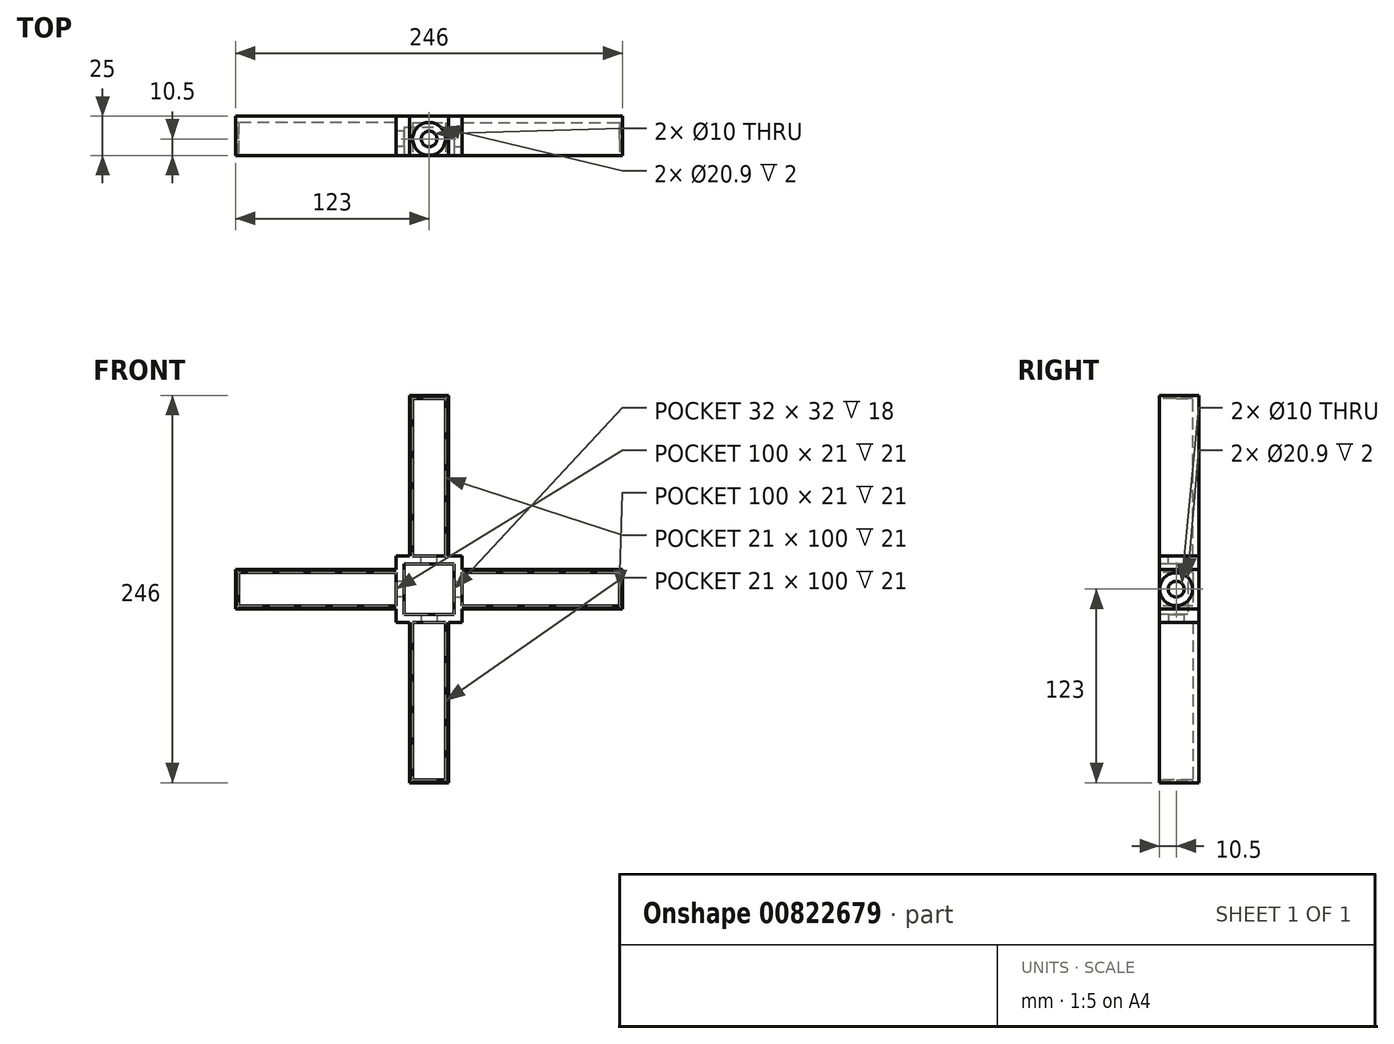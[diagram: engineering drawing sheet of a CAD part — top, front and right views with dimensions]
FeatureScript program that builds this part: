
annotation { "Feature Type Name" : "Feature", "Feature Type Description" : "" }
export const myFeature = defineFeature(function(context is Context, id is Id, definition is map)
    precondition{}
    {
        {
            var Q0;
            Q0=qCreatedBy(makeId("Front.planeOp"),FACE);
            var sketch = newSketch(context, id + "F0", { "sketchPlane" : qUnion([Q0])});
            skLineSegment(sketch, "E0.bottom", {"start": v(-21, 21) * mm, "end": v(21, 21) * mm});
            skLineSegment(sketch, "E0.top", {"start": v(-21, -21) * mm, "end": v(21, -21) * mm});
            skLineSegment(sketch, "E0.left", {"start": v(-21, 21) * mm, "end": v(-21, -21) * mm});
            skLineSegment(sketch, "E0.right", {"start": v(21, 21) * mm, "end": v(21, -21) * mm});
            skPoint(sketch, "E0.middle", {"position": v(0, 0) * mm});
            skLineSegment(sketch, "E1.bottom", {"start": v(-16, 16) * mm, "end": v(16, 16) * mm});
            skLineSegment(sketch, "E1.top", {"start": v(-16, -16) * mm, "end": v(16, -16) * mm});
            skLineSegment(sketch, "E1.left", {"start": v(-16, 16) * mm, "end": v(-16, -16) * mm});
            skLineSegment(sketch, "E1.right", {"start": v(16, 16) * mm, "end": v(16, -16) * mm});
            skSolve(sketch);
        }
        {
            var Q0;
            Q0=qCreatedBy(makeId("Front.planeOp"),FACE);
            var sketch = newSketch(context, id + "F1", { "sketchPlane" : qUnion([Q0])});
            skLineSegment(sketch, "E2.bottom", {"start": v(-12.5, -21) * mm, "end": v(12.5, -21) * mm});
            skLineSegment(sketch, "E2.top", {"start": v(-12.5, -123) * mm, "end": v(12.5, -123) * mm});
            skLineSegment(sketch, "E2.left", {"start": v(-12.5, -21) * mm, "end": v(-12.5, -123) * mm});
            skLineSegment(sketch, "E2.right", {"start": v(12.5, -21) * mm, "end": v(12.5, -123) * mm});
            skSolve(sketch);
        }
        {
            var Q0;
            Q0=qCreatedBy(makeId("Front.planeOp"),FACE);
            var sketch = newSketch(context, id + "F2", { "sketchPlane" : qUnion([Q0])});
            skLineSegment(sketch, "E3.bottom", {"start": v(-21, 12.5) * mm, "end": v(-123, 12.5) * mm});
            skLineSegment(sketch, "E3.top", {"start": v(-21, -12.5) * mm, "end": v(-123, -12.5) * mm});
            skLineSegment(sketch, "E3.left", {"start": v(-21, 12.5) * mm, "end": v(-21, -12.5) * mm});
            skLineSegment(sketch, "E3.right", {"start": v(-123, 12.5) * mm, "end": v(-123, -12.5) * mm});
            skSolve(sketch);
        }
        {
            var Q0;
            Q0=qCreatedBy(makeId("Front.planeOp"),FACE);
            var sketch = newSketch(context, id + "F3", { "sketchPlane" : qUnion([Q0])});
            skLineSegment(sketch, "E4.bottom", {"start": v(21, 12.5) * mm, "end": v(123, 12.5) * mm});
            skLineSegment(sketch, "E4.top", {"start": v(21, -12.5) * mm, "end": v(123, -12.5) * mm});
            skLineSegment(sketch, "E4.left", {"start": v(21, 12.5) * mm, "end": v(21, -12.5) * mm});
            skLineSegment(sketch, "E4.right", {"start": v(123, 12.5) * mm, "end": v(123, -12.5) * mm});
            skSolve(sketch);
        }
        {
            var Q0;
            Q0=qCreatedBy(makeId("Front.planeOp"),FACE);
            var sketch = newSketch(context, id + "F4", { "sketchPlane" : qUnion([Q0])});
            skLineSegment(sketch, "E5.bottom", {"start": v(-12.5, 21) * mm, "end": v(12.5, 21) * mm});
            skLineSegment(sketch, "E5.top", {"start": v(-12.5, 123) * mm, "end": v(12.5, 123) * mm});
            skLineSegment(sketch, "E5.left", {"start": v(-12.5, 21) * mm, "end": v(-12.5, 123) * mm});
            skLineSegment(sketch, "E5.right", {"start": v(12.5, 21) * mm, "end": v(12.5, 123) * mm});
            skSolve(sketch);
        }
        {
            var Q0;
            Q0 = qSketchRegion(id + "F0", true);
            var Q1;
            Q1=makeQuery(id+"F0.imprint","IMPRINT",FACE,{"disambiguationData":[TD([[makeQuery(id+"F0.imprint","IMPRINT",EDGE,{"derivedFrom":sQuery(id+"F0.wireOp",EDGE,"E1.bottom")}),-1.0]])]});
            extrude(context, id + "F5", {"entities" : qUnion([Q0, Q1]), "depth" : 25 * mm, "offsetDistance" : 25 * mm});
        }
        {
            var Q0;
            Q0 = qSketchRegion(id + "F1", true);
            var Q1;
            Q1 = qSketchRegion(id + "F2", true);
            var Q2;
            Q2 = qSketchRegion(id + "F3", true);
            var Q3;
            Q3 = qSketchRegion(id + "F4", true);
            extrude(context, id + "F6", {"entities" : qUnion([Q0, Q1, Q2, Q3]), "operationType" : NewBodyOperationType.ADD, "depth" : 25 * mm, "offsetDistance" : 25 * mm});
        }
        {
            var Q0;
            Q0=makeQuery(id+"F6.boolean.opBoolean","MERGE",FACE,{"derivedFrom":[makeQuery(id+"F5.opExtrude","CAP_FACE",FACE,{"disambiguationData":[OSD([sQuery(id+"F0.wireOp",EDGE,"E0.bottom"),sQuery(id+"F0.wireOp",EDGE,"E0.top"),sQuery(id+"F0.wireOp",EDGE,"E0.left"),sQuery(id+"F0.wireOp",EDGE,"E0.right")])],"isStart":false}),makeQuery(id+"F6.opExtrude","CAP_FACE",FACE,{"disambiguationData":[OSD([sQuery(id+"F1.wireOp",EDGE,"E2.bottom"),sQuery(id+"F1.wireOp",EDGE,"E2.top"),sQuery(id+"F1.wireOp",EDGE,"E2.left"),sQuery(id+"F1.wireOp",EDGE,"E2.right")])],"isStart":false}),makeQuery(id+"F6.opExtrude","CAP_FACE",FACE,{"disambiguationData":[OSD([sQuery(id+"F2.wireOp",EDGE,"E3.bottom"),sQuery(id+"F2.wireOp",EDGE,"E3.top"),sQuery(id+"F2.wireOp",EDGE,"E3.left"),sQuery(id+"F2.wireOp",EDGE,"E3.right")])],"isStart":false}),makeQuery(id+"F6.opExtrude","CAP_FACE",FACE,{"disambiguationData":[OSD([sQuery(id+"F3.wireOp",EDGE,"E4.bottom"),sQuery(id+"F3.wireOp",EDGE,"E4.top"),sQuery(id+"F3.wireOp",EDGE,"E4.left"),sQuery(id+"F3.wireOp",EDGE,"E4.right")])],"isStart":false}),makeQuery(id+"F6.opExtrude","CAP_FACE",FACE,{"disambiguationData":[OSD([sQuery(id+"F4.wireOp",EDGE,"E5.bottom"),sQuery(id+"F4.wireOp",EDGE,"E5.top"),sQuery(id+"F4.wireOp",EDGE,"E5.left"),sQuery(id+"F4.wireOp",EDGE,"E5.right")])],"isStart":false})]});
            var sketch = newSketch(context, id + "F7", { "sketchPlane" : qUnion([Q0])});
            skLineSegment(sketch, "E6.bottom", {"start": v(-16, 16) * mm, "end": v(16, 16) * mm});
            skLineSegment(sketch, "E6.top", {"start": v(-16, -16) * mm, "end": v(16, -16) * mm});
            skLineSegment(sketch, "E6.left", {"start": v(-16, 16) * mm, "end": v(-16, -16) * mm});
            skLineSegment(sketch, "E6.right", {"start": v(16, 16) * mm, "end": v(16, -16) * mm});
            skPoint(sketch, "E6.middle", {"position": v(0, 0) * mm});
            skSolve(sketch);
        }
        {
            var Q0;
            Q0=makeQuery(id+"F7.imprint","IMPRINT",FACE,{"disambiguationData":[TD([[makeQuery(id+"F7.imprint","IMPRINT",EDGE,{"derivedFrom":sQuery(id+"F7.wireOp",EDGE,"E6.bottom")}),-1.0]])]});
            extrude(context, id + "F8", {"entities" : qUnion([Q0]), "operationType" : NewBodyOperationType.REMOVE, "oppositeDirection" : true, "depth" : 18 * mm, "offsetDistance" : 25 * mm});
        }
        {
            var Q0;
            Q0=makeQuery(id+"F6.boolean.opBoolean","MERGE",FACE,{"derivedFrom":[makeQuery(id+"F5.opExtrude","CAP_FACE",FACE,{"disambiguationData":[OSD([sQuery(id+"F0.wireOp",EDGE,"E0.bottom"),sQuery(id+"F0.wireOp",EDGE,"E0.top"),sQuery(id+"F0.wireOp",EDGE,"E0.left"),sQuery(id+"F0.wireOp",EDGE,"E0.right")])],"isStart":false}),makeQuery(id+"F6.opExtrude","CAP_FACE",FACE,{"disambiguationData":[OSD([sQuery(id+"F1.wireOp",EDGE,"E2.bottom"),sQuery(id+"F1.wireOp",EDGE,"E2.top"),sQuery(id+"F1.wireOp",EDGE,"E2.left"),sQuery(id+"F1.wireOp",EDGE,"E2.right")])],"isStart":false}),makeQuery(id+"F6.opExtrude","CAP_FACE",FACE,{"disambiguationData":[OSD([sQuery(id+"F2.wireOp",EDGE,"E3.bottom"),sQuery(id+"F2.wireOp",EDGE,"E3.top"),sQuery(id+"F2.wireOp",EDGE,"E3.left"),sQuery(id+"F2.wireOp",EDGE,"E3.right")])],"isStart":false}),makeQuery(id+"F6.opExtrude","CAP_FACE",FACE,{"disambiguationData":[OSD([sQuery(id+"F3.wireOp",EDGE,"E4.bottom"),sQuery(id+"F3.wireOp",EDGE,"E4.top"),sQuery(id+"F3.wireOp",EDGE,"E4.left"),sQuery(id+"F3.wireOp",EDGE,"E4.right")])],"isStart":false}),makeQuery(id+"F6.opExtrude","CAP_FACE",FACE,{"disambiguationData":[OSD([sQuery(id+"F4.wireOp",EDGE,"E5.bottom"),sQuery(id+"F4.wireOp",EDGE,"E5.top"),sQuery(id+"F4.wireOp",EDGE,"E5.left"),sQuery(id+"F4.wireOp",EDGE,"E5.right")])],"isStart":false})]});
            var sketch = newSketch(context, id + "F9", { "sketchPlane" : qUnion([Q0])});
            skLineSegment(sketch, "E7.bottom", {"start": v(-21, 10.5) * mm, "end": v(-121, 10.5) * mm});
            skLineSegment(sketch, "E7.top", {"start": v(-21, -10.5) * mm, "end": v(-121, -10.5) * mm});
            skLineSegment(sketch, "E7.left", {"start": v(-21, 10.5) * mm, "end": v(-21, -10.5) * mm});
            skLineSegment(sketch, "E7.right", {"start": v(-121, 10.5) * mm, "end": v(-121, -10.5) * mm});
            skSolve(sketch);
        }
        {
            var Q0;
            Q0=makeQuery(id+"F9.imprint","IMPRINT",FACE,{"disambiguationData":[TD([[makeQuery(id+"F9.imprint","IMPRINT",EDGE,{"derivedFrom":sQuery(id+"F9.wireOp",EDGE,"E7.bottom")}),1.0]])]});
            extrude(context, id + "F10", {"entities" : qUnion([Q0]), "operationType" : NewBodyOperationType.REMOVE, "oppositeDirection" : true, "depth" : 21 * mm, "offsetDistance" : 25 * mm});
        }
        {
            var Q0;
            Q0=makeQuery(id+"F6.boolean.opBoolean","MERGE",FACE,{"derivedFrom":[makeQuery(id+"F5.opExtrude","CAP_FACE",FACE,{"disambiguationData":[OSD([sQuery(id+"F0.wireOp",EDGE,"E0.bottom"),sQuery(id+"F0.wireOp",EDGE,"E0.top"),sQuery(id+"F0.wireOp",EDGE,"E0.left"),sQuery(id+"F0.wireOp",EDGE,"E0.right")])],"isStart":false}),makeQuery(id+"F6.opExtrude","CAP_FACE",FACE,{"disambiguationData":[OSD([sQuery(id+"F1.wireOp",EDGE,"E2.bottom"),sQuery(id+"F1.wireOp",EDGE,"E2.top"),sQuery(id+"F1.wireOp",EDGE,"E2.left"),sQuery(id+"F1.wireOp",EDGE,"E2.right")])],"isStart":false}),makeQuery(id+"F6.opExtrude","CAP_FACE",FACE,{"disambiguationData":[OSD([sQuery(id+"F2.wireOp",EDGE,"E3.bottom"),sQuery(id+"F2.wireOp",EDGE,"E3.top"),sQuery(id+"F2.wireOp",EDGE,"E3.left"),sQuery(id+"F2.wireOp",EDGE,"E3.right")])],"isStart":false}),makeQuery(id+"F6.opExtrude","CAP_FACE",FACE,{"disambiguationData":[OSD([sQuery(id+"F3.wireOp",EDGE,"E4.bottom"),sQuery(id+"F3.wireOp",EDGE,"E4.top"),sQuery(id+"F3.wireOp",EDGE,"E4.left"),sQuery(id+"F3.wireOp",EDGE,"E4.right")])],"isStart":false}),makeQuery(id+"F6.opExtrude","CAP_FACE",FACE,{"disambiguationData":[OSD([sQuery(id+"F4.wireOp",EDGE,"E5.bottom"),sQuery(id+"F4.wireOp",EDGE,"E5.top"),sQuery(id+"F4.wireOp",EDGE,"E5.left"),sQuery(id+"F4.wireOp",EDGE,"E5.right")])],"isStart":false})]});
            var sketch = newSketch(context, id + "F11", { "sketchPlane" : qUnion([Q0])});
            skLineSegment(sketch, "E8.bottom", {"start": v(21, 10.5) * mm, "end": v(121, 10.5) * mm});
            skLineSegment(sketch, "E8.top", {"start": v(21, -10.5) * mm, "end": v(121, -10.5) * mm});
            skLineSegment(sketch, "E8.left", {"start": v(21, 10.5) * mm, "end": v(21, -10.5) * mm});
            skLineSegment(sketch, "E8.right", {"start": v(121, 10.5) * mm, "end": v(121, -10.5) * mm});
            skSolve(sketch);
        }
        {
            var Q0;
            Q0=makeQuery(id+"F11.imprint","IMPRINT",FACE,{"disambiguationData":[TD([[makeQuery(id+"F11.imprint","IMPRINT",EDGE,{"derivedFrom":sQuery(id+"F11.wireOp",EDGE,"E8.bottom")}),-1.0]])]});
            extrude(context, id + "F12", {"entities" : qUnion([Q0]), "operationType" : NewBodyOperationType.REMOVE, "oppositeDirection" : true, "depth" : 21 * mm, "offsetDistance" : 25 * mm});
        }
        {
            var Q0;
            Q0=makeQuery(id+"F6.boolean.opBoolean","MERGE",FACE,{"derivedFrom":[makeQuery(id+"F5.opExtrude","CAP_FACE",FACE,{"disambiguationData":[OSD([sQuery(id+"F0.wireOp",EDGE,"E0.bottom"),sQuery(id+"F0.wireOp",EDGE,"E0.top"),sQuery(id+"F0.wireOp",EDGE,"E0.left"),sQuery(id+"F0.wireOp",EDGE,"E0.right")])],"isStart":false}),makeQuery(id+"F6.opExtrude","CAP_FACE",FACE,{"disambiguationData":[OSD([sQuery(id+"F1.wireOp",EDGE,"E2.bottom"),sQuery(id+"F1.wireOp",EDGE,"E2.top"),sQuery(id+"F1.wireOp",EDGE,"E2.left"),sQuery(id+"F1.wireOp",EDGE,"E2.right")])],"isStart":false}),makeQuery(id+"F6.opExtrude","CAP_FACE",FACE,{"disambiguationData":[OSD([sQuery(id+"F2.wireOp",EDGE,"E3.bottom"),sQuery(id+"F2.wireOp",EDGE,"E3.top"),sQuery(id+"F2.wireOp",EDGE,"E3.left"),sQuery(id+"F2.wireOp",EDGE,"E3.right")])],"isStart":false}),makeQuery(id+"F6.opExtrude","CAP_FACE",FACE,{"disambiguationData":[OSD([sQuery(id+"F3.wireOp",EDGE,"E4.bottom"),sQuery(id+"F3.wireOp",EDGE,"E4.top"),sQuery(id+"F3.wireOp",EDGE,"E4.left"),sQuery(id+"F3.wireOp",EDGE,"E4.right")])],"isStart":false}),makeQuery(id+"F6.opExtrude","CAP_FACE",FACE,{"disambiguationData":[OSD([sQuery(id+"F4.wireOp",EDGE,"E5.bottom"),sQuery(id+"F4.wireOp",EDGE,"E5.top"),sQuery(id+"F4.wireOp",EDGE,"E5.left"),sQuery(id+"F4.wireOp",EDGE,"E5.right")])],"isStart":false})]});
            var sketch = newSketch(context, id + "F13", { "sketchPlane" : qUnion([Q0])});
            skLineSegment(sketch, "E9.bottom", {"start": v(-10.5, 21) * mm, "end": v(10.5, 21) * mm});
            skLineSegment(sketch, "E9.top", {"start": v(-10.5, 121) * mm, "end": v(10.5, 121) * mm});
            skLineSegment(sketch, "E9.left", {"start": v(-10.5, 21) * mm, "end": v(-10.5, 121) * mm});
            skLineSegment(sketch, "E9.right", {"start": v(10.5, 21) * mm, "end": v(10.5, 121) * mm});
            skSolve(sketch);
        }
        {
            var Q0;
            Q0=makeQuery(id+"F13.imprint","IMPRINT",FACE,{"disambiguationData":[TD([[makeQuery(id+"F13.imprint","IMPRINT",EDGE,{"derivedFrom":sQuery(id+"F13.wireOp",EDGE,"E9.bottom")}),1.0]])]});
            extrude(context, id + "F14", {"entities" : qUnion([Q0]), "operationType" : NewBodyOperationType.REMOVE, "oppositeDirection" : true, "depth" : 21 * mm, "offsetDistance" : 25 * mm});
        }
        {
            var Q0;
            Q0=makeQuery(id+"F6.boolean.opBoolean","MERGE",FACE,{"derivedFrom":[makeQuery(id+"F5.opExtrude","CAP_FACE",FACE,{"disambiguationData":[OSD([sQuery(id+"F0.wireOp",EDGE,"E0.bottom"),sQuery(id+"F0.wireOp",EDGE,"E0.top"),sQuery(id+"F0.wireOp",EDGE,"E0.left"),sQuery(id+"F0.wireOp",EDGE,"E0.right")])],"isStart":false}),makeQuery(id+"F6.opExtrude","CAP_FACE",FACE,{"disambiguationData":[OSD([sQuery(id+"F1.wireOp",EDGE,"E2.bottom"),sQuery(id+"F1.wireOp",EDGE,"E2.top"),sQuery(id+"F1.wireOp",EDGE,"E2.left"),sQuery(id+"F1.wireOp",EDGE,"E2.right")])],"isStart":false}),makeQuery(id+"F6.opExtrude","CAP_FACE",FACE,{"disambiguationData":[OSD([sQuery(id+"F2.wireOp",EDGE,"E3.bottom"),sQuery(id+"F2.wireOp",EDGE,"E3.top"),sQuery(id+"F2.wireOp",EDGE,"E3.left"),sQuery(id+"F2.wireOp",EDGE,"E3.right")])],"isStart":false}),makeQuery(id+"F6.opExtrude","CAP_FACE",FACE,{"disambiguationData":[OSD([sQuery(id+"F3.wireOp",EDGE,"E4.bottom"),sQuery(id+"F3.wireOp",EDGE,"E4.top"),sQuery(id+"F3.wireOp",EDGE,"E4.left"),sQuery(id+"F3.wireOp",EDGE,"E4.right")])],"isStart":false}),makeQuery(id+"F6.opExtrude","CAP_FACE",FACE,{"disambiguationData":[OSD([sQuery(id+"F4.wireOp",EDGE,"E5.bottom"),sQuery(id+"F4.wireOp",EDGE,"E5.top"),sQuery(id+"F4.wireOp",EDGE,"E5.left"),sQuery(id+"F4.wireOp",EDGE,"E5.right")])],"isStart":false})]});
            var sketch = newSketch(context, id + "F15", { "sketchPlane" : qUnion([Q0])});
            skLineSegment(sketch, "E10.bottom", {"start": v(-10.5, -21) * mm, "end": v(10.5, -21) * mm});
            skLineSegment(sketch, "E10.top", {"start": v(-10.5, -121) * mm, "end": v(10.5, -121) * mm});
            skLineSegment(sketch, "E10.left", {"start": v(-10.5, -21) * mm, "end": v(-10.5, -121) * mm});
            skLineSegment(sketch, "E10.right", {"start": v(10.5, -21) * mm, "end": v(10.5, -121) * mm});
            skSolve(sketch);
        }
        {
            var Q0;
            Q0=makeQuery(id+"F15.imprint","IMPRINT",FACE,{"disambiguationData":[TD([[makeQuery(id+"F15.imprint","IMPRINT",EDGE,{"derivedFrom":sQuery(id+"F15.wireOp",EDGE,"E10.bottom")}),-1.0]])]});
            extrude(context, id + "F16", {"entities" : qUnion([Q0]), "operationType" : NewBodyOperationType.REMOVE, "oppositeDirection" : true, "depth" : 21 * mm, "offsetDistance" : 25 * mm});
        }
        {
            var Q0;
            Q0=makeQuery(id+"F12.boolean.opBoolean","COPY",FACE,{"derivedFrom":makeQuery(id+"F12.opExtrude","SWEPT_FACE",FACE,{"disambiguationData":[OSD([sQuery(id+"F11.wireOp",EDGE,"E8.left")])]})});
            var sketch = newSketch(context, id + "F17", { "sketchPlane" : qUnion([Q0])});
            skCircle(sketch, "E11", {"center": v(-14.5, 0) * mm, "radius": 5 * mm});
            skSolve(sketch);
        }
        {
            var Q0;
            Q0=sQuery(id+"F17.wireOp",VERTEX,"E11.center");
            var Q1;
            Q1=makeQuery(id+"F5.opExtrude","SWEPT_BODY",BODY,{"disambiguationData":[OSD([sQuery(id+"F0.wireOp",EDGE,"E0.bottom"),sQuery(id+"F0.wireOp",EDGE,"E0.top"),sQuery(id+"F0.wireOp",EDGE,"E0.left"),sQuery(id+"F0.wireOp",EDGE,"E0.right")])]});
            hole(context, id + "F18", {"style" : HoleStyle.SIMPLE, "endStyle" : HoleEndStyle.BLIND, "holeDiameter" : 10 * mm, "majorDiameter" : 5 * mm, "holeDepth" : 11 * mm, "isTappedThrough" : true, "tappedDepth" : 12 * mm, "tapClearance" : 3, "locations" : qUnion([Q0]), "scope" : qUnion([Q1])});
        }
        {
            var Q0;
            Q0=makeQuery(id+"F16.boolean.opBoolean","COPY",FACE,{"derivedFrom":makeQuery(id+"F16.opExtrude","SWEPT_FACE",FACE,{"disambiguationData":[OSD([sQuery(id+"F15.wireOp",EDGE,"E10.bottom")])]})});
            var sketch = newSketch(context, id + "F19", { "sketchPlane" : qUnion([Q0])});
            skCircle(sketch, "E12", {"center": v(0, 14.5) * mm, "radius": 5 * mm});
            skSolve(sketch);
        }
        {
            var Q0;
            Q0=sQuery(id+"F19.wireOp",VERTEX,"E12.center");
            var Q1;
            Q1=makeQuery(id+"F5.opExtrude","SWEPT_BODY",BODY,{"disambiguationData":[OSD([sQuery(id+"F0.wireOp",EDGE,"E0.bottom"),sQuery(id+"F0.wireOp",EDGE,"E0.top"),sQuery(id+"F0.wireOp",EDGE,"E0.left"),sQuery(id+"F0.wireOp",EDGE,"E0.right")])]});
            hole(context, id + "F20", {"style" : HoleStyle.SIMPLE, "endStyle" : HoleEndStyle.BLIND, "holeDiameter" : 10 * mm, "majorDiameter" : 5 * mm, "holeDepth" : 11 * mm, "isTappedThrough" : true, "tappedDepth" : 12 * mm, "tapClearance" : 3, "locations" : qUnion([Q0]), "scope" : qUnion([Q1])});
        }
        {
            var Q0;
            Q0=makeQuery(id+"F14.boolean.opBoolean","COPY",FACE,{"derivedFrom":makeQuery(id+"F14.opExtrude","SWEPT_FACE",FACE,{"disambiguationData":[OSD([sQuery(id+"F13.wireOp",EDGE,"E9.bottom")])]})});
            var sketch = newSketch(context, id + "F21", { "sketchPlane" : qUnion([Q0])});
            skCircle(sketch, "E13", {"center": v(0, -14.5) * mm, "radius": 5 * mm});
            skSolve(sketch);
        }
        {
            var Q0;
            Q0=sQuery(id+"F21.wireOp",VERTEX,"E13.center");
            var Q1;
            Q1=makeQuery(id+"F5.opExtrude","SWEPT_BODY",BODY,{"disambiguationData":[OSD([sQuery(id+"F0.wireOp",EDGE,"E0.bottom"),sQuery(id+"F0.wireOp",EDGE,"E0.top"),sQuery(id+"F0.wireOp",EDGE,"E0.left"),sQuery(id+"F0.wireOp",EDGE,"E0.right")])]});
            hole(context, id + "F22", {"style" : HoleStyle.SIMPLE, "endStyle" : HoleEndStyle.BLIND, "holeDiameter" : 10 * mm, "majorDiameter" : 5 * mm, "holeDepth" : 11 * mm, "isTappedThrough" : true, "tappedDepth" : 12 * mm, "tapClearance" : 3, "locations" : qUnion([Q0]), "scope" : qUnion([Q1])});
        }
        {
            var Q0;
            Q0=makeQuery(id+"F10.boolean.opBoolean","COPY",FACE,{"derivedFrom":makeQuery(id+"F10.opExtrude","SWEPT_FACE",FACE,{"disambiguationData":[OSD([sQuery(id+"F9.wireOp",EDGE,"E7.left")])]})});
            var sketch = newSketch(context, id + "F23", { "sketchPlane" : qUnion([Q0])});
            skCircle(sketch, "E14", {"center": v(14.5, 0) * mm, "radius": 5 * mm});
            skSolve(sketch);
        }
        {
            var Q0;
            Q0=sQuery(id+"F23.wireOp",VERTEX,"E14.center");
            var Q1;
            Q1=makeQuery(id+"F5.opExtrude","SWEPT_BODY",BODY,{"disambiguationData":[OSD([sQuery(id+"F0.wireOp",EDGE,"E0.bottom"),sQuery(id+"F0.wireOp",EDGE,"E0.top"),sQuery(id+"F0.wireOp",EDGE,"E0.left"),sQuery(id+"F0.wireOp",EDGE,"E0.right")])]});
            hole(context, id + "F24", {"style" : HoleStyle.SIMPLE, "endStyle" : HoleEndStyle.BLIND, "holeDiameter" : 10 * mm, "majorDiameter" : 5 * mm, "holeDepth" : 11 * mm, "isTappedThrough" : true, "tappedDepth" : 12 * mm, "tapClearance" : 3, "locations" : qUnion([Q0]), "scope" : qUnion([Q1])});
        }
        {
            var Q0;
            Q0=makeQuery(id+"F6.opExtrude","SWEPT_FACE",FACE,{"disambiguationData":[OSD([sQuery(id+"F2.wireOp",EDGE,"E3.right")])]});
            var sketch = newSketch(context, id + "F25", { "sketchPlane" : qUnion([Q0])});
            skCircle(sketch, "E15", {"center": v(14.5, 0) * mm, "radius": 10.5 * mm});
            skSolve(sketch);
        }
        {
            var Q0;
            Q0=sQuery(id+"F25.wireOp",VERTEX,"E15.center");
            var Q1;
            Q1=makeQuery(id+"F5.opExtrude","SWEPT_BODY",BODY,{"disambiguationData":[OSD([sQuery(id+"F0.wireOp",EDGE,"E0.bottom"),sQuery(id+"F0.wireOp",EDGE,"E0.top"),sQuery(id+"F0.wireOp",EDGE,"E0.left"),sQuery(id+"F0.wireOp",EDGE,"E0.right")])]});
            hole(context, id + "F26", {"style" : HoleStyle.SIMPLE, "endStyle" : HoleEndStyle.BLIND, "holeDiameter" : 20.9 * mm, "majorDiameter" : 5 * mm, "holeDepth" : 3 * mm, "isTappedThrough" : true, "tappedDepth" : 12 * mm, "tapClearance" : 3, "locations" : qUnion([Q0]), "scope" : qUnion([Q1])});
        }
        {
            var Q0;
            Q0=makeQuery(id+"F6.opExtrude","SWEPT_FACE",FACE,{"disambiguationData":[OSD([sQuery(id+"F4.wireOp",EDGE,"E5.top")])]});
            var sketch = newSketch(context, id + "F27", { "sketchPlane" : qUnion([Q0])});
            skCircle(sketch, "E16", {"center": v(0, -14.5) * mm, "radius": 10.5 * mm});
            skSolve(sketch);
        }
        {
            var Q0;
            Q0=sQuery(id+"F27.wireOp",VERTEX,"E16.center");
            var Q1;
            Q1=makeQuery(id+"F5.opExtrude","SWEPT_BODY",BODY,{"disambiguationData":[OSD([sQuery(id+"F0.wireOp",EDGE,"E0.bottom"),sQuery(id+"F0.wireOp",EDGE,"E0.top"),sQuery(id+"F0.wireOp",EDGE,"E0.left"),sQuery(id+"F0.wireOp",EDGE,"E0.right")])]});
            hole(context, id + "F28", {"style" : HoleStyle.SIMPLE, "endStyle" : HoleEndStyle.BLIND, "holeDiameter" : 20.9 * mm, "majorDiameter" : 5 * mm, "holeDepth" : 3 * mm, "isTappedThrough" : true, "tappedDepth" : 12 * mm, "tapClearance" : 3, "locations" : qUnion([Q0]), "scope" : qUnion([Q1])});
        }
        {
            var Q0;
            Q0=makeQuery(id+"F6.opExtrude","SWEPT_FACE",FACE,{"disambiguationData":[OSD([sQuery(id+"F1.wireOp",EDGE,"E2.top")])]});
            var sketch = newSketch(context, id + "F29", { "sketchPlane" : qUnion([Q0])});
            skCircle(sketch, "E17", {"center": v(0, 14.5) * mm, "radius": 10.5 * mm});
            skSolve(sketch);
        }
        {
            var Q0;
            Q0=sQuery(id+"F29.wireOp",VERTEX,"E17.center");
            var Q1;
            Q1=makeQuery(id+"F5.opExtrude","SWEPT_BODY",BODY,{"disambiguationData":[OSD([sQuery(id+"F0.wireOp",EDGE,"E0.bottom"),sQuery(id+"F0.wireOp",EDGE,"E0.top"),sQuery(id+"F0.wireOp",EDGE,"E0.left"),sQuery(id+"F0.wireOp",EDGE,"E0.right")])]});
            hole(context, id + "F30", {"style" : HoleStyle.SIMPLE, "endStyle" : HoleEndStyle.BLIND, "holeDiameter" : 20.9 * mm, "majorDiameter" : 5 * mm, "holeDepth" : 3 * mm, "isTappedThrough" : true, "tappedDepth" : 12 * mm, "tapClearance" : 3, "locations" : qUnion([Q0]), "scope" : qUnion([Q1])});
        }
        {
            var Q0;
            Q0=makeQuery(id+"F6.opExtrude","SWEPT_FACE",FACE,{"disambiguationData":[OSD([sQuery(id+"F3.wireOp",EDGE,"E4.right")])]});
            var sketch = newSketch(context, id + "F31", { "sketchPlane" : qUnion([Q0])});
            skCircle(sketch, "E18", {"center": v(-14.5, 0) * mm, "radius": 10.5 * mm});
            skSolve(sketch);
        }
        {
            var Q0;
            Q0=sQuery(id+"F31.wireOp",VERTEX,"E18.center");
            var Q1;
            Q1=makeQuery(id+"F5.opExtrude","SWEPT_BODY",BODY,{"disambiguationData":[OSD([sQuery(id+"F0.wireOp",EDGE,"E0.bottom"),sQuery(id+"F0.wireOp",EDGE,"E0.top"),sQuery(id+"F0.wireOp",EDGE,"E0.left"),sQuery(id+"F0.wireOp",EDGE,"E0.right")])]});
            hole(context, id + "F32", {"style" : HoleStyle.SIMPLE, "endStyle" : HoleEndStyle.BLIND, "holeDiameter" : 20.9 * mm, "majorDiameter" : 5 * mm, "holeDepth" : 3 * mm, "isTappedThrough" : true, "tappedDepth" : 12 * mm, "tapClearance" : 3, "locations" : qUnion([Q0]), "scope" : qUnion([Q1])});
        }
    });
